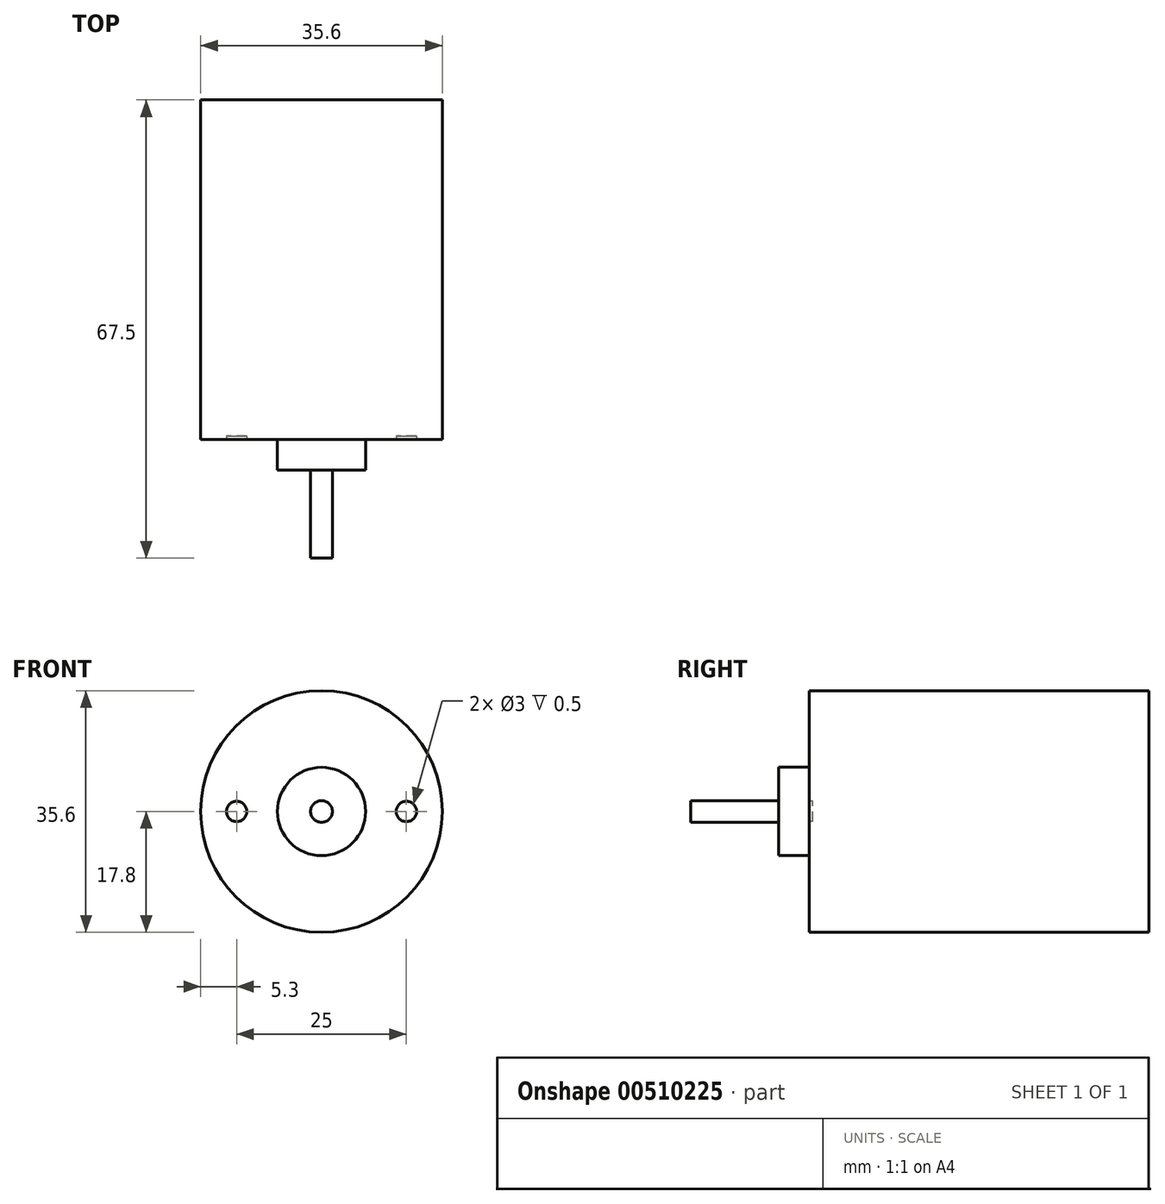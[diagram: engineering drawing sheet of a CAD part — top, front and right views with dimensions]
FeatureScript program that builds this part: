
annotation { "Feature Type Name" : "Feature", "Feature Type Description" : "" }
export const myFeature = defineFeature(function(context is Context, id is Id, definition is map)
    precondition{}
    {
        {
            var Q0;
            Q0=qCreatedBy(makeId("Front.planeOp"),FACE);
            var sketch = newSketch(context, id + "F0", { "sketchPlane" : qUnion([Q0])});
            skCircle(sketch, "E0", {"center": v(0, 0) * mm, "radius": 17.8 * mm});
            skSolve(sketch);
        }
        {
            var Q0;
            Q0=makeQuery(id+"F0.imprint","IMPRINT",FACE,{"disambiguationData":[TD([[makeQuery(id+"F0.imprint","IMPRINT",EDGE,{"derivedFrom":sQuery(id+"F0.wireOp",EDGE,"E0")}),1.0]])]});
            extrude(context, id + "F1", {"entities" : qUnion([Q0]), "depth" : 50 * mm});
        }
        {
            var Q0;
            Q0=makeQuery(id+"F1.opExtrude","CAP_FACE",FACE,{"disambiguationData":[OSD([sQuery(id+"F0.wireOp",EDGE,"E0")])],"isStart":false});
            var sketch = newSketch(context, id + "F2", { "sketchPlane" : qUnion([Q0])});
            skCircle(sketch, "E1", {"center": v(0, 0) * mm, "radius": 6.5 * mm});
            skSolve(sketch);
        }
        {
            var Q0;
            Q0=makeQuery(id+"F2.imprint","IMPRINT",FACE,{"disambiguationData":[TD([[makeQuery(id+"F2.imprint","IMPRINT",EDGE,{"derivedFrom":sQuery(id+"F2.wireOp",EDGE,"E1")}),1.0]])]});
            extrude(context, id + "F3", {"entities" : qUnion([Q0]), "operationType" : NewBodyOperationType.ADD, "depth" : 4.5 * mm});
        }
        {
            var Q0;
            Q0=makeQuery(id+"F3.opExtrude","CAP_FACE",FACE,{"disambiguationData":[OSD([sQuery(id+"F2.wireOp",EDGE,"E1")])],"isStart":false});
            var sketch = newSketch(context, id + "F4", { "sketchPlane" : qUnion([Q0])});
            skCircle(sketch, "E2", {"center": v(0, 0) * mm, "radius": 1.6 * mm});
            skSolve(sketch);
        }
        {
            var Q0;
            Q0=makeQuery(id+"F4.imprint","IMPRINT",FACE,{"disambiguationData":[TD([[makeQuery(id+"F4.imprint","IMPRINT",EDGE,{"derivedFrom":sQuery(id+"F4.wireOp",EDGE,"E2")}),1.0]])]});
            extrude(context, id + "F5", {"entities" : qUnion([Q0]), "operationType" : NewBodyOperationType.ADD, "depth" : 13 * mm});
        }
        {
            var Q0;
            Q0=makeQuery(id+"F1.opExtrude","CAP_FACE",FACE,{"disambiguationData":[OSD([sQuery(id+"F0.wireOp",EDGE,"E0")])],"isStart":false});
            var sketch = newSketch(context, id + "F6", { "sketchPlane" : qUnion([Q0])});
            skCircle(sketch, "E3", {"center": v(0, 0) * mm, "radius": 12.5 * mm, "construction": true});
            skCircle(sketch, "E4", {"center": v(-12.5, 0) * mm, "radius": 1.5 * mm});
            skCircle(sketch, "E5", {"center": v(12.5, 0) * mm, "radius": 1.5 * mm});
            skSolve(sketch);
        }
        {
            var Q0;
            Q0=makeQuery(id+"F6.imprint","IMPRINT",FACE,{"disambiguationData":[TD([[makeQuery(id+"F6.imprint","IMPRINT",EDGE,{"derivedFrom":sQuery(id+"F6.wireOp",EDGE,"E4")}),1.0]])]});
            var Q1;
            Q1=makeQuery(id+"F6.imprint","IMPRINT",FACE,{"disambiguationData":[TD([[makeQuery(id+"F6.imprint","IMPRINT",EDGE,{"derivedFrom":sQuery(id+"F6.wireOp",EDGE,"E5")}),1.0]])]});
            extrude(context, id + "F7", {"entities" : qUnion([Q0, Q1]), "operationType" : NewBodyOperationType.REMOVE, "oppositeDirection" : true, "depth" : .5 * mm});
        }
    });
